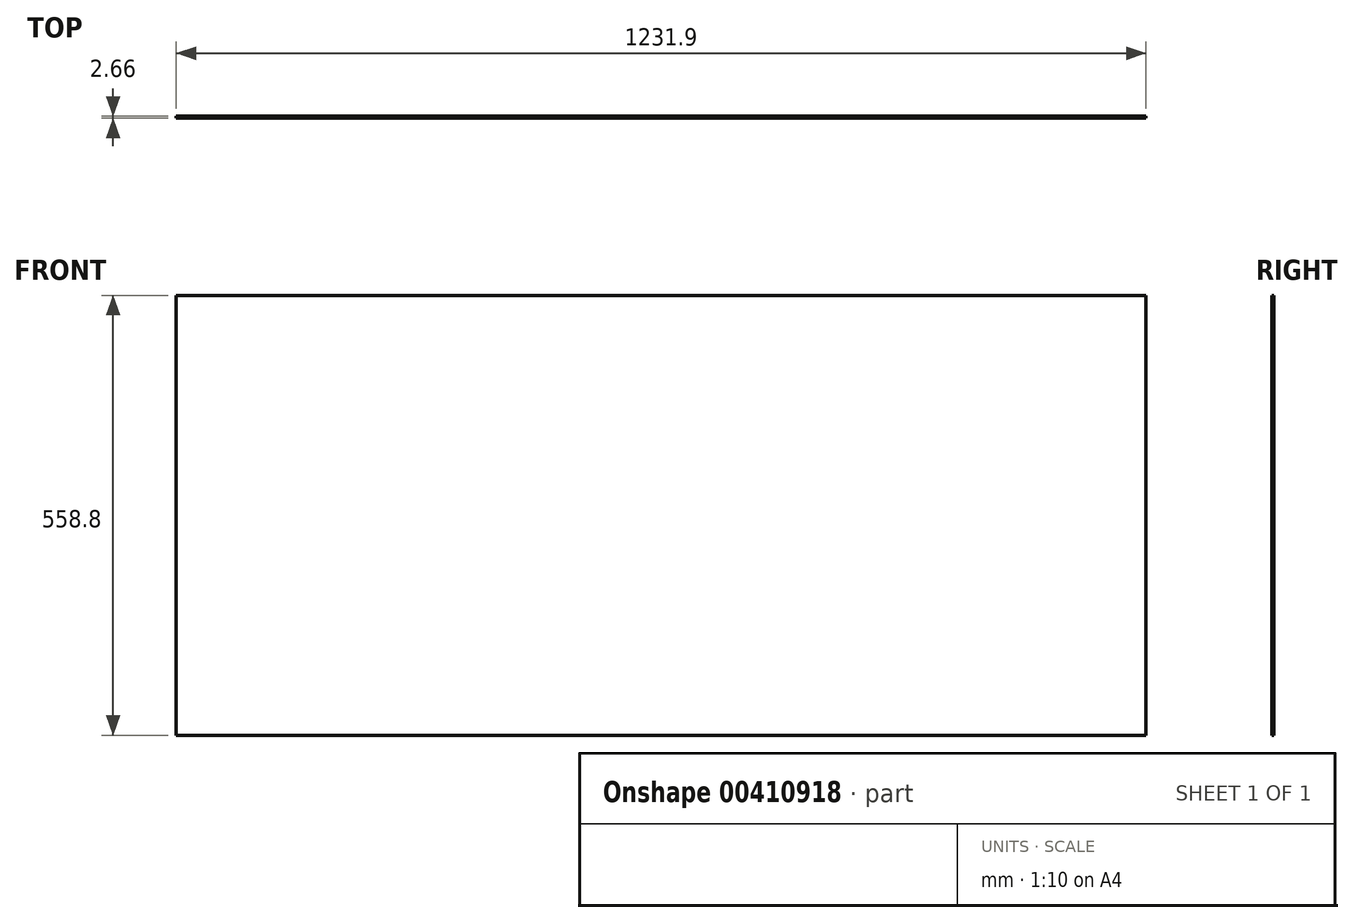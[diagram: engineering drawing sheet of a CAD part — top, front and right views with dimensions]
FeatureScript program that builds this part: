
annotation { "Feature Type Name" : "Feature", "Feature Type Description" : "" }
export const myFeature = defineFeature(function(context is Context, id is Id, definition is map)
    precondition{}
    {
        {
            var Q0;
            Q0=qCreatedBy(makeId("Front.planeOp"),FACE);
            var sketch = newSketch(context, id + "F0", { "sketchPlane" : qUnion([Q0])});
            skLineSegment(sketch, "E0.bottom", {"start": v(0, 0) * mm, "end": v(1231.9, 0) * mm});
            skLineSegment(sketch, "E0.top", {"start": v(0, -558.8) * mm, "end": v(1231.9, -558.8) * mm});
            skLineSegment(sketch, "E0.left", {"start": v(0, 0) * mm, "end": v(0, -558.8) * mm});
            skLineSegment(sketch, "E0.right", {"start": v(1231.9, 0) * mm, "end": v(1231.9, -558.8) * mm});
            skSolve(sketch);
        }
        {
            var Q0;
            Q0 = qSketchRegion(id + "F0", true);
            extrude(context, id + "F1", {"entities" : qUnion([Q0]), "depth" : 2.66 * mm});
        }
    });
